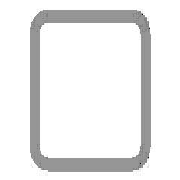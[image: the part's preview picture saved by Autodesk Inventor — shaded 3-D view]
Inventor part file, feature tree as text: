
AUTODESK INVENTOR PART (.ipt)
format: ipt  version: 2023 (Build 270158000, 158)  size: 225,280 bytes
history: native  units: mm (DEFAULTED — no unit token found)
features: other x14, sketch x5, extrude x3, plane x1
ambient origin geometry x8: Origin, YZ Plane, XZ Plane, XY Plane, X Axis, Y Axis, Z Axis, Center Point
bodies: Solid1 (feature_tree)
feature tree (23):
  parser-record x1  (decoder bookkeeping rows leaked as tree rows — omitted from the tree; the rows remain in map.json)
  other  "Driven Length"
  other  "Płaszczyzna początkowa"
  other  "Płaszczyzna końcowa"
  extrude  "Bryła"  TaperAngle=0.0deg  [1 undecoded]
  other  "Płaszczyzna konstrukcyjna4"
  other  "Płaszczyzna konstrukcyjna5"
  other  "Płaszczyzna konstrukcyjna6"
  extrude  "Wyciągnięcie proste2"  Depth=4.0mm
  other  "Utwórz kombinację1"
  other  "Płaszczyzna konstrukcyjna7"
  other  "Płaszczyzna konstrukcyjna8"
  other  "Płaszczyzna konstrukcyjna9"
  extrude  "Wyciągnięcie proste3"  Depth=4.0mm
  other  "Utwórz kombinację2"
  sketch  "Szkic"
  sketch  "Sketch3"  dims[d3=800.0mm d4=0.0mm]
  plane  "Work Plane3"
  sketch  "Sketch4"  dims[d7=4.0mm d10=40.0mm d11=40.0mm d12=3.2mm d13=-0.0mm d14=800.0mm d15=20.0mm d16=20.0mm d17=90.0deg d18=800.0mm d19=0.13mm d20=0.0mm d21=0.13mm d22=0.0mm]
  sketch  "Szkic5"
  other  "Bryła2"
  sketch  "Szkic6"
  other  "Bryła3"
note: 1 required parameter value undecoded (feature->parameter linkage not recoverable at this tier; creation-order binding heuristic only, values carry confidence <= 0.55)
